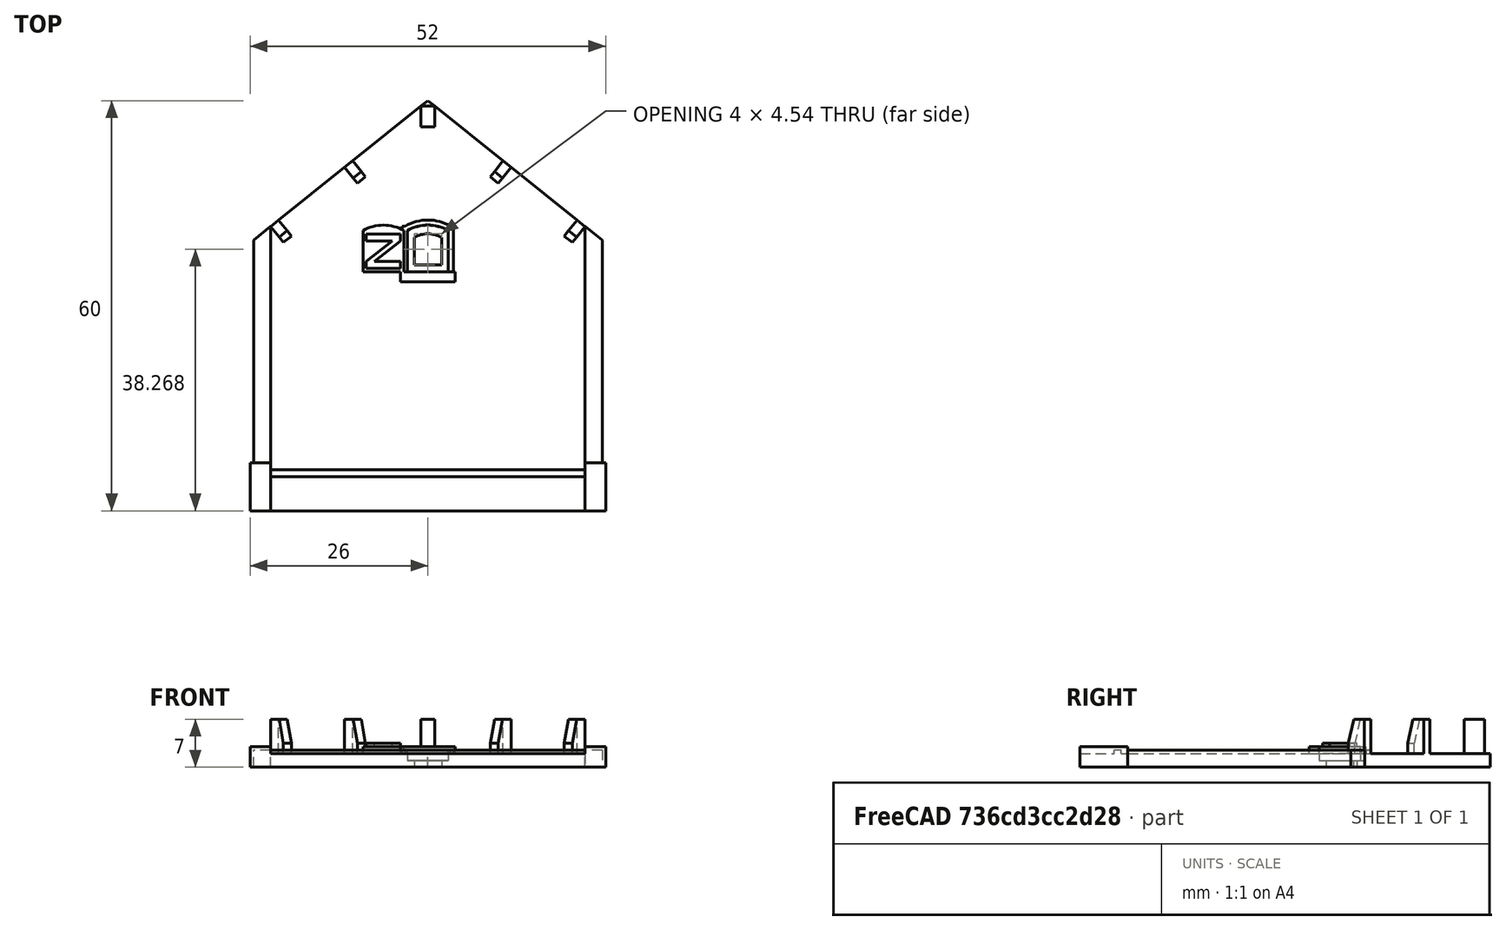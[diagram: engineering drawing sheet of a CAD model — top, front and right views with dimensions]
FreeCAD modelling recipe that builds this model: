
FCSTD DOCUMENT  (FreeCAD 0.16R6698 (Git))
Label: 2_P_Face_Arriere
License: All rights reserved
LicenseURL: http://fr.wikipedia.org/wiki/<copyright redacted>
objects: Part::FeaturePython×2, Part::MultiFuse×1
note: 3 computed .brp shape members not serialized (recipe doc carries the construction recipe); baked Part::Feature solids carry a one-line shape summary decoded from their .brp

FEATURE [Part::FeaturePython] face_arriere_v2_01  label="2_1_Face_Arriere"  # a2plus imported part (geometry in sourceFile) (typed FeaturePython)
  fixedPosition = true
  sourceFile = <userpath>/Bureau/Dropbox/3D/Objet-francis/FreeCad-Modelisme-Maison-Garde-Barriere/Lib/2_1_Face_Arriere.fcstd
  timeLastImport = 1.49651e+09
  updateColors = true
FEATURE [Part::FeaturePython] volet_fenestrou_01  label="1_3_Volet_Fenestrou"  # a2plus imported part (geometry in sourceFile) (typed FeaturePython)
  Placement = pos=(-6.5,18,2) rot=(0,0,1;0rad)
  fixedPosition = false
  sourceFile = <userpath>/Bureau/Dropbox/3D/Objet-francis/FreeCad-Modelisme-Maison-Garde-Barriere/Lib/1_3_Volet_Fenestrou.fcstd
  timeLastImport = 1.49633e+09
  updateColors = true
FEATURE [Part::MultiFuse] Fusion
  Shapes = -> [face_arriere_v2_01,volet_fenestrou_01]
